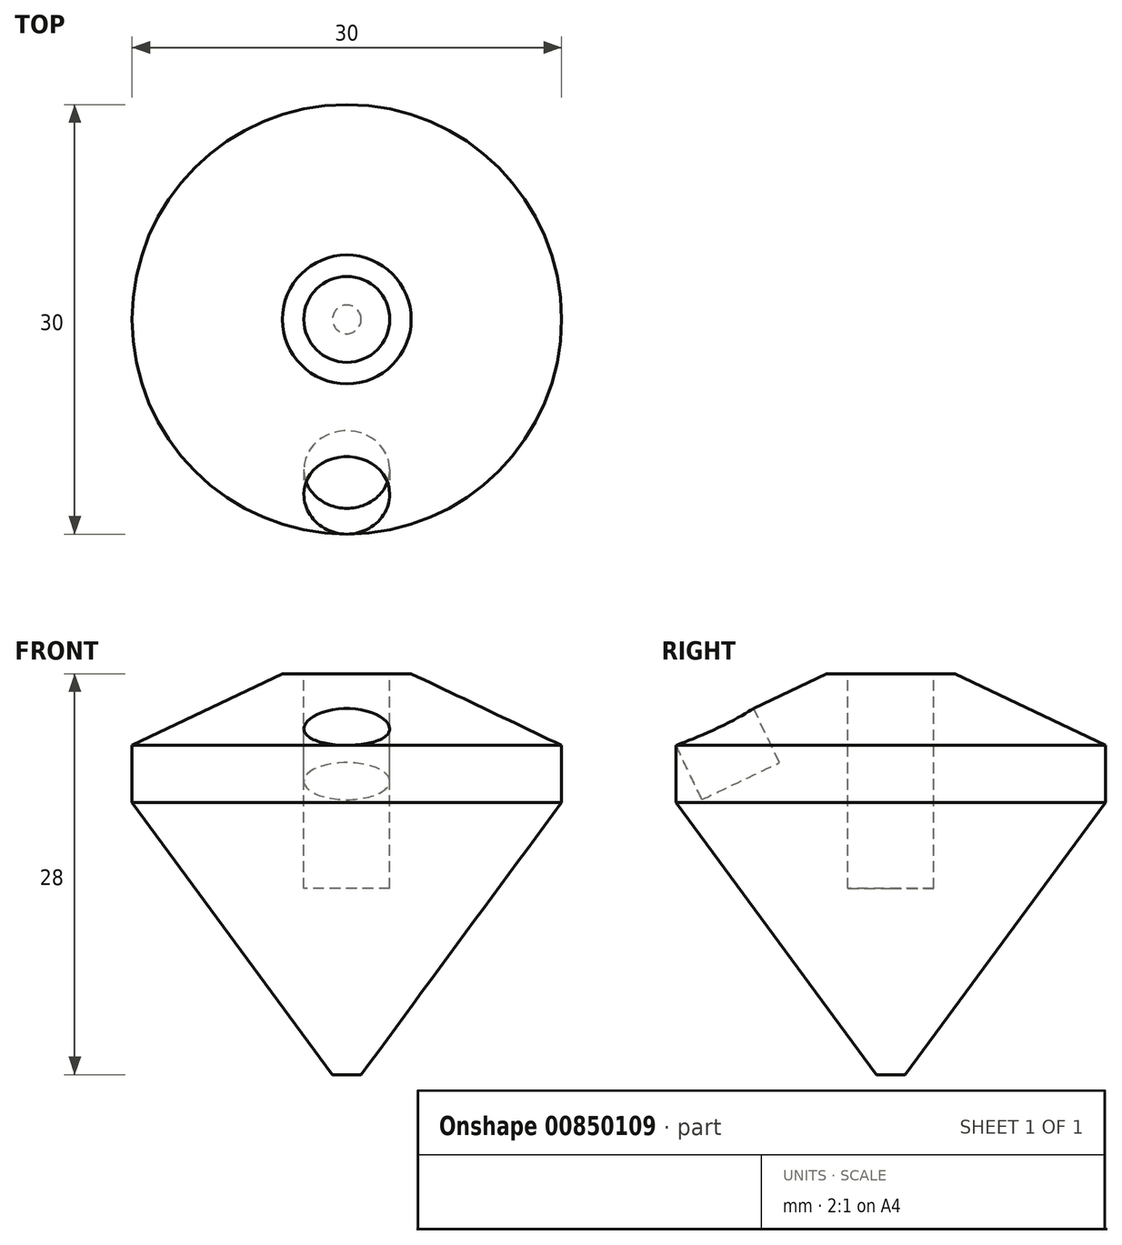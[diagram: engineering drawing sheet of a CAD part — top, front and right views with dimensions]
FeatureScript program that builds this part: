
annotation { "Feature Type Name" : "Feature", "Feature Type Description" : "" }
export const myFeature = defineFeature(function(context is Context, id is Id, definition is map)
    precondition{}
    {
        {
            var Q0;
            Q0=qCreatedBy(makeId("Front.planeOp"),FACE);
            var sketch = newSketch(context, id + "F0", { "sketchPlane" : qUnion([Q0])});
            skLineSegment(sketch, "E0", {"start": v(0, 15) * mm, "end": v(4.5, 15) * mm});
            skLineSegment(sketch, "E1", {"start": v(4.5, 15) * mm, "end": v(15, 10) * mm});
            skLineSegment(sketch, "E2", {"start": v(15, 10) * mm, "end": v(15, 6) * mm});
            skLineSegment(sketch, "E3", {"start": v(15, 6) * mm, "end": v(1, -13) * mm});
            skLineSegment(sketch, "E4", {"start": v(1, -13) * mm, "end": v(0, -13) * mm});
            skLineSegment(sketch, "E5", {"start": v(0, -13) * mm, "end": v(0, 15) * mm});
            skSolve(sketch);
        }
        {
            var Q0;
            Q0=qCreatedBy(makeId("Front.planeOp"),FACE);
            var sketch = newSketch(context, id + "F1", { "sketchPlane" : qUnion([Q0])});
            skLineSegment(sketch, "E6", {"start": v(0, 38.45) * mm, "end": v(0, -41.4) * mm, "construction": true});
            skSolve(sketch);
        }
        {
            var Q0;
            Q0 = qSketchRegion(id + "F0", true);
            var Q1;
            Q1=sQuery(id+"F1.wireOp",EDGE,"E6");
            revolve(context, id + "F2", {"surfaceOperationType" : NewSurfaceOperationType.NEW, "entities" : qUnion([Q0]), "axis" : qUnion([Q1]), "revolveType" : RevolveType.FULL});
        }
        {
            var Q0;
            Q0=qCreatedBy(makeId("Right.planeOp"),FACE);
            var Q1;
            Q1=qCreatedBy(makeId("Right.planeOp"),FACE);
            var sketch = newSketch(context, id + "F3", { "sketchPlane" : qUnion([Q0, Q1])});
            skLineSegment(sketch, "E7", {"start": v(-14.55, 10.21) * mm, "end": v(-4.05, 15.21) * mm});
            skSolve(sketch);
        }
        {
            var Q0;
            Q0=sQuery(id+"F3.wireOp",EDGE,"E7");
            cPlane(context, id + "F4", {"entities" : qUnion([Q0]), "cplaneType" : CPlaneType.LINE_ANGLE, "offset" : 25 * mm, "angle" : 0 * degree, "width" : 150 * mm, "height" : 150 * mm});
        }
        {
            var Q0;
            Q0=qCreatedBy(id+"F4.planeOp",FACE);
            var Q1;
            Q1=qCreatedBy(id+"F4.planeOp",FACE);
            var sketch = newSketch(context, id + "F5", { "sketchPlane" : qUnion([Q0, Q1])});
            skCircle(sketch, "E8", {"center": v(0, -6.24) * mm, "radius": 3 * mm});
            skSolve(sketch);
        }
        {
            var Q0;
            Q0 = qSketchRegion(id + "F5", true);
            extrude(context, id + "F6", {"entities" : qUnion([Q0]), "operationType" : NewBodyOperationType.REMOVE, "oppositeDirection" : true, "depth" : 4.2 * mm, "offsetDistance" : 25 * mm});
        }
        {
            var Q0;
            Q0=qCreatedBy(makeId("Front.planeOp"),FACE);
            var Q1;
            Q1=qCreatedBy(makeId("Front.planeOp"),FACE);
            var sketch = newSketch(context, id + "F7", { "sketchPlane" : qUnion([Q0, Q1])});
            skLineSegment(sketch, "E9", {"start": v(0, 129.59) * mm, "end": v(0, -144.1) * mm, "construction": true});
            skSolve(sketch);
        }
        {
            var Q0;
            Q0=makeQuery(id+"F2.opRevolve","SWEPT_FACE",FACE,{"disambiguationData":[OSD([sQuery(id+"F0.wireOp",EDGE,"E0")])]});
            var sketch = newSketch(context, id + "F8", { "sketchPlane" : qUnion([Q0])});
            skCircle(sketch, "E10", {"center": v(0, 0) * mm, "radius": 3 * mm});
            skSolve(sketch);
        }
        {
            var Q0;
            Q0 = qSketchRegion(id + "F8", true);
            extrude(context, id + "F9", {"entities" : qUnion([Q0]), "operationType" : NewBodyOperationType.REMOVE, "oppositeDirection" : true, "depth" : 15 * mm, "offsetDistance" : 25 * mm});
        }
    });
